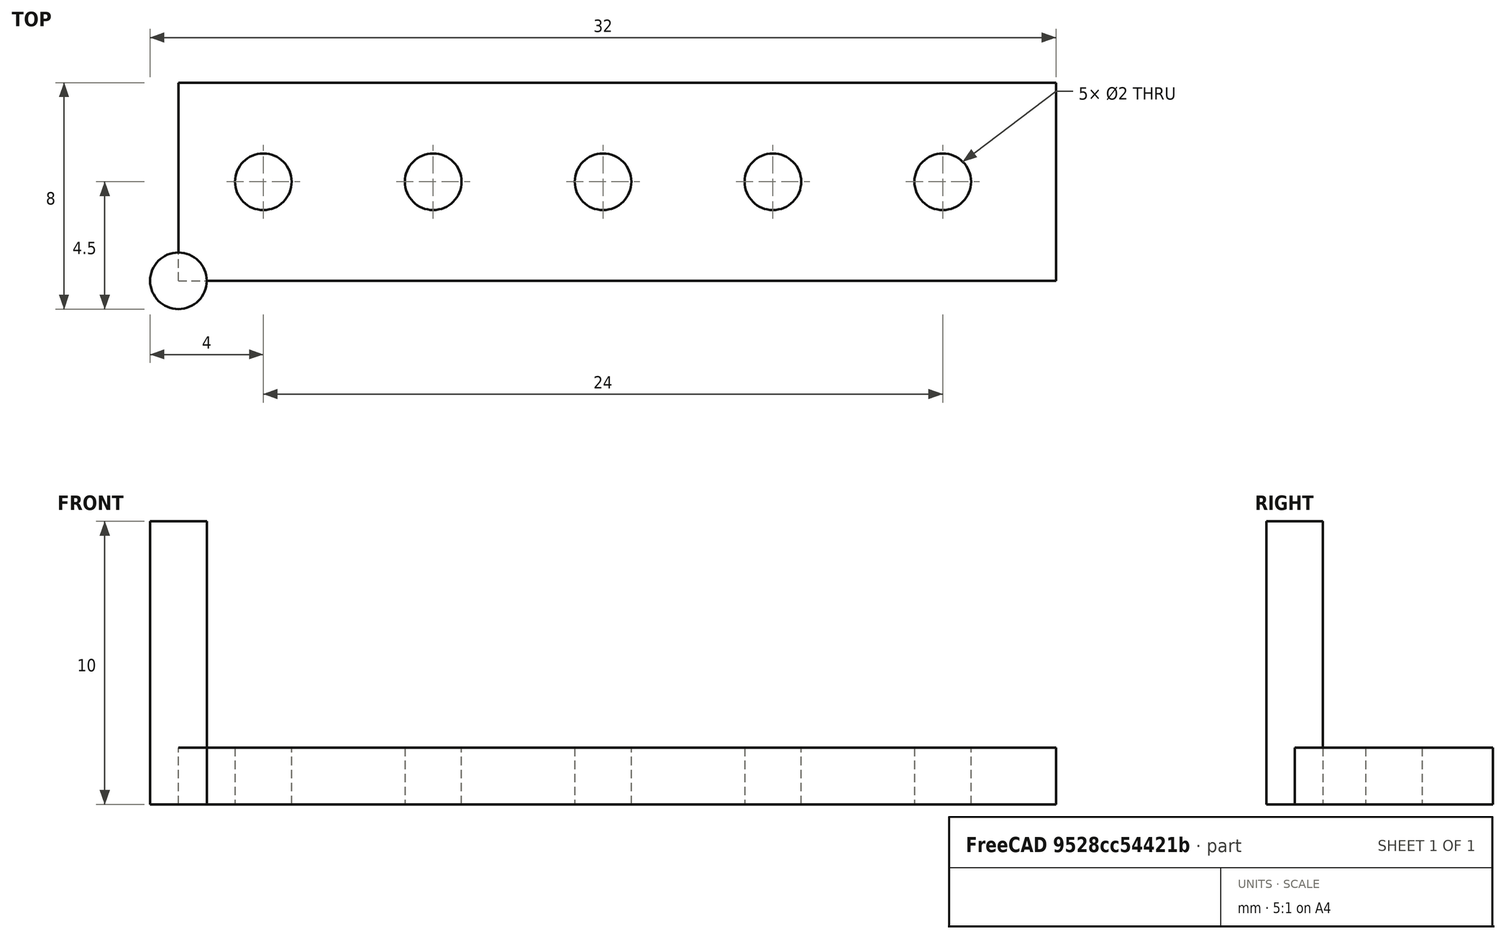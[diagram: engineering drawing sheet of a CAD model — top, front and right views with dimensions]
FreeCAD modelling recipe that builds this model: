
FCSTD DOCUMENT  (FreeCAD 1.0R39319 (Git))
Label: ojt1_t10r01_array.cylinder
License: All rights reserved
LicenseURL: https://en.wikipedia.org/wiki/All_rights_reserved
objects: Part::Box×1, Part::Cylinder×1, Part::FeaturePython×1, Part::Cut×1
note: 3 computed .brp shape members not serialized (recipe doc carries the construction recipe); baked Part::Feature solids carry a one-line shape summary decoded from their .brp

FEATURE [Part::Box] Box  label="Cub"
  AttacherType = Attacher::AttachEngine3D
  Height = 2
  Length = 31
  Width = 7
FEATURE [Part::Cylinder] Cylinder  label="Cilindre"
  Angle = 360
  AttacherType = Attacher::AttachEngine3D
  FirstAngle = 0
  Height = 10
  Radius = 1
  SecondAngle = 0
FEATURE [Part::FeaturePython] Array  # Draft array (typed FeaturePython)
  AlwaysSyncPlacement = false
  Angle = 360
  ArrayType = 0
  Axis = (0,0,1)
  Base = -> Cylinder
  Center = (0,0,0)
  Count = 10
  ExpandArray = false
  Fuse = false
  IntervalAxis = (0,0,0)
  IntervalX = (6,0,0)
  IntervalY = (0,0,0)
  IntervalZ = (0,0,100)
  NumberCircles = 3
  NumberPolar = 5
  NumberX = 5
  NumberY = 2
  NumberZ = 1
  Placement = pos=(3,3.5,-4) rot=(0,0,1;0rad)
  PlacementList = 10 placements: [(0,0,0),(0,0,0),(6,0,0),(6,0,0),(12,0,0),(12,0,0),(18,0,0),(18,0,0),(24,0,0),(24,0,0)]
  RadialDistance = 50
  ScaleList = (10) [(1,1,1),(1,1,1),(1,1,1),(1,1,1),(1,1,1),(1,1,1),(1,1,1),(1,1,1),(1,1,1),(1,1,1)]
  Symmetry = 1
  TangentialDistance = 25
FEATURE [Part::Cut] Cut
  Base = -> Box
  Refine = true
  Tool = -> Array
